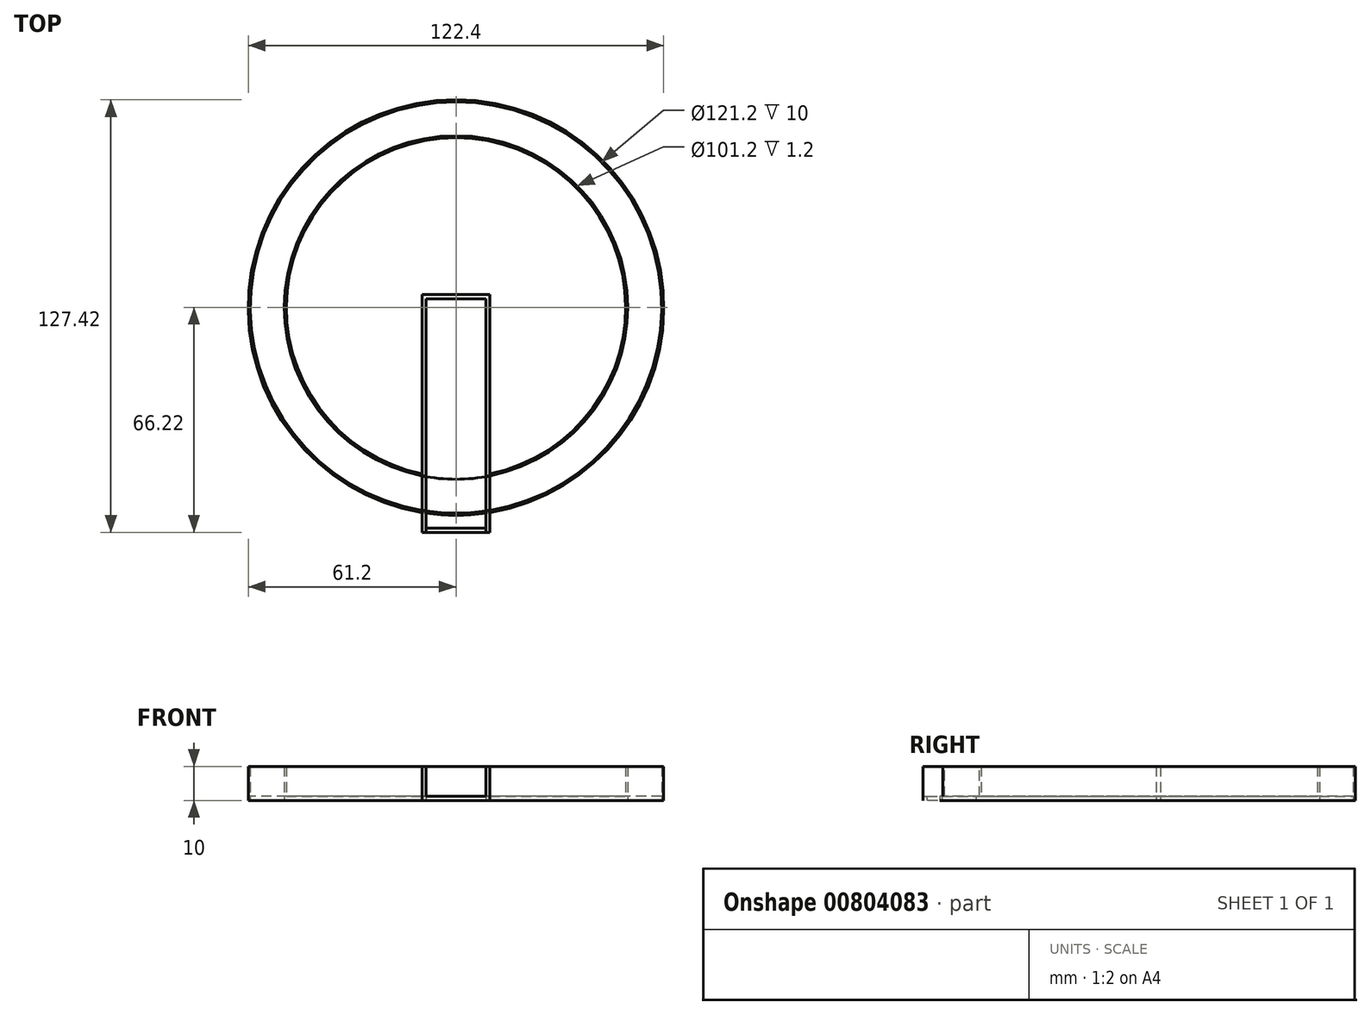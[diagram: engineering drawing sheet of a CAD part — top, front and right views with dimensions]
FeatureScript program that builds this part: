
annotation { "Feature Type Name" : "Feature", "Feature Type Description" : "" }
export const myFeature = defineFeature(function(context is Context, id is Id, definition is map)
    precondition{}
    {
        {
            var Q0;
            Q0=qCreatedBy(makeId("Top.planeOp"),FACE);
            var sketch = newSketch(context, id + "F0", { "sketchPlane" : qUnion([Q0])});
            skCircle(sketch, "E0", {"center": v(0, 0) * mm, "radius": 50 * mm});
            skCircle(sketch, "E1", {"center": v(0, 0) * mm, "radius": 50.6 * mm});
            skSolve(sketch);
        }
        {
            var Q0;
            Q0=qCreatedBy(makeId("Top.planeOp"),FACE);
            var sketch = newSketch(context, id + "F1", { "sketchPlane" : qUnion([Q0])});
            skCircle(sketch, "E2", {"center": v(0, 0) * mm, "radius": 50 * mm});
            skSolve(sketch);
        }
        {
            var Q0;
            Q0=makeQuery(id+"F0.imprint","IMPRINT",FACE,{"disambiguationData":[TD([[makeQuery(id+"F0.imprint","IMPRINT",EDGE,{"derivedFrom":sQuery(id+"F0.wireOp",EDGE,"E0")}),-1.0]])]});
            extrude(context, id + "F2", {"entities" : qUnion([Q0]), "depth" : 10 * mm, "offsetDistance" : 25 * mm});
        }
        {
            var Q0;
            Q0=makeQuery(id+"F1.imprint","IMPRINT",FACE,{"disambiguationData":[TD([[makeQuery(id+"F1.imprint","IMPRINT",EDGE,{"derivedFrom":sQuery(id+"F1.wireOp",EDGE,"E2")}),1.0]])]});
            extrude(context, id + "F3", {"entities" : qUnion([Q0]), "operationType" : NewBodyOperationType.ADD, "depth" : 1.2 * mm, "offsetDistance" : 25 * mm});
        }
        {
            var Q0;
            Q0=qCreatedBy(makeId("Top.planeOp"),FACE);
            var sketch = newSketch(context, id + "F4", { "sketchPlane" : qUnion([Q0])});
            skCircle(sketch, "E3", {"center": v(0, 0) * mm, "radius": 60.6 * mm});
            skCircle(sketch, "E4", {"center": v(0, 0) * mm, "radius": 61.2 * mm});
            skSolve(sketch);
        }
        {
            var Q0;
            Q0=qCreatedBy(makeId("Top.planeOp"),FACE);
            var sketch = newSketch(context, id + "F5", { "sketchPlane" : qUnion([Q0])});
            skCircle(sketch, "E5", {"center": v(0, 0) * mm, "radius": 60.6 * mm});
            skCircle(sketch, "E6", {"center": v(0, 0) * mm, "radius": 50.6 * mm});
            skSolve(sketch);
        }
        {
            var Q0;
            Q0=makeQuery(id+"F4.imprint","IMPRINT",FACE,{"disambiguationData":[TD([[makeQuery(id+"F4.imprint","IMPRINT",EDGE,{"derivedFrom":sQuery(id+"F4.wireOp",EDGE,"E3")}),-1.0]])]});
            extrude(context, id + "F6", {"entities" : qUnion([Q0]), "depth" : 10 * mm, "offsetDistance" : 25 * mm});
        }
        {
            var Q0;
            Q0=makeQuery(id+"F5.imprint","IMPRINT",FACE,{"disambiguationData":[TD([[makeQuery(id+"F5.imprint","IMPRINT",EDGE,{"derivedFrom":sQuery(id+"F5.wireOp",EDGE,"E5")}),1.0]])]});
            extrude(context, id + "F7", {"entities" : qUnion([Q0]), "depth" : 1.2 * mm, "offsetDistance" : 25 * mm});
        }
        {
            var Q0;
            Q0=qCreatedBy(makeId("Front.planeOp"),FACE);
            var sketch = newSketch(context, id + "F8", { "sketchPlane" : qUnion([Q0])});
            skLineSegment(sketch, "E7.bottom", {"start": v(-10, 10) * mm, "end": v(10, 10) * mm});
            skLineSegment(sketch, "E7.top", {"start": v(-10, 1.2) * mm, "end": v(10, 1.2) * mm});
            skLineSegment(sketch, "E7.left", {"start": v(-10, 10) * mm, "end": v(-10, 1.2) * mm});
            skLineSegment(sketch, "E7.right", {"start": v(10, 10) * mm, "end": v(10, 1.2) * mm});
            skPoint(sketch, "E7.middle", {"position": v(0, 5.6) * mm});
            skSolve(sketch);
        }
        {
            var Q0;
            Q0=makeQuery(id+"F8.imprint","IMPRINT",FACE,{"disambiguationData":[TD([[makeQuery(id+"F8.imprint","IMPRINT",EDGE,{"derivedFrom":sQuery(id+"F8.wireOp",EDGE,"E7.bottom")}),-1.0]])]});
            extrude(context, id + "F9", {"entities" : qUnion([Q0]), "operationType" : NewBodyOperationType.REMOVE, "depth" : 80 * mm, "offsetDistance" : 25 * mm});
        }
        {
            var Q0;
            Q0=qCreatedBy(makeId("Top.planeOp"),FACE);
            var sketch = newSketch(context, id + "F10", { "sketchPlane" : qUnion([Q0])});
            skLineSegment(sketch, "E8.bottom", {"start": v(-10, -66.22) * mm, "end": v(10, -66.22) * mm});
            skLineSegment(sketch, "E8.top", {"start": v(-10, 3.78) * mm, "end": v(10, 3.78) * mm});
            skLineSegment(sketch, "E8.left", {"start": v(-10, -66.22) * mm, "end": v(-10, 3.78) * mm});
            skLineSegment(sketch, "E8.right", {"start": v(10, -66.22) * mm, "end": v(10, 3.78) * mm});
            skPoint(sketch, "E8.middle", {"position": v(0, -31.22) * mm});
            skLineSegment(sketch, "E9.bottom", {"start": v(-8.8, 2.58) * mm, "end": v(8.8, 2.58) * mm});
            skLineSegment(sketch, "E9.top", {"start": v(-8.8, -65.02) * mm, "end": v(8.8, -65.02) * mm});
            skLineSegment(sketch, "E9.left", {"start": v(-8.8, 2.58) * mm, "end": v(-8.8, -65.02) * mm});
            skLineSegment(sketch, "E9.right", {"start": v(8.8, 2.58) * mm, "end": v(8.8, -65.02) * mm});
            skSolve(sketch);
        }
        {
            var Q0;
            Q0=makeQuery(id+"F10.imprint","IMPRINT",FACE,{"disambiguationData":[TD([[makeQuery(id+"F10.imprint","IMPRINT",EDGE,{"derivedFrom":sQuery(id+"F10.wireOp",EDGE,"E8.bottom")}),1.0]])]});
            extrude(context, id + "F11", {"entities" : qUnion([Q0]), "depth" : 10 * mm, "offsetDistance" : 25 * mm});
        }
        {
            var Q0;
            Q0=qCreatedBy(makeId("Top.planeOp"),FACE);
            var sketch = newSketch(context, id + "F12", { "sketchPlane" : qUnion([Q0])});
            skLineSegment(sketch, "E10.bottom", {"start": v(-8.8, -65.02) * mm, "end": v(8.8, -65.02) * mm});
            skLineSegment(sketch, "E10.top", {"start": v(-8.8, 2.58) * mm, "end": v(8.8, 2.58) * mm});
            skLineSegment(sketch, "E10.left", {"start": v(-8.8, -65.02) * mm, "end": v(-8.8, 2.58) * mm});
            skLineSegment(sketch, "E10.right", {"start": v(8.8, -65.02) * mm, "end": v(8.8, 2.58) * mm});
            skPoint(sketch, "E10.middle", {"position": v(0, -31.22) * mm});
            skSolve(sketch);
        }
        {
            var Q0;
            Q0=makeQuery(id+"F12.imprint","IMPRINT",FACE,{"disambiguationData":[TD([[makeQuery(id+"F12.imprint","IMPRINT",EDGE,{"derivedFrom":sQuery(id+"F12.wireOp",EDGE,"E10.bottom")}),1.0]])]});
            extrude(context, id + "F13", {"entities" : qUnion([Q0]), "depth" : 1.2 * mm, "offsetDistance" : 25 * mm});
        }
        {
            var Q0;
            Q0=qCreatedBy(makeId("Right.planeOp"),FACE);
            var sketch = newSketch(context, id + "F14", { "sketchPlane" : qUnion([Q0])});
            skLineSegment(sketch, "E11.bottom", {"start": v(-59.77, 10) * mm, "end": v(-49.6, 10) * mm});
            skLineSegment(sketch, "E11.top", {"start": v(-59.77, 1.2) * mm, "end": v(-49.6, 1.2) * mm});
            skLineSegment(sketch, "E11.left", {"start": v(-59.77, 10) * mm, "end": v(-59.77, 1.2) * mm});
            skLineSegment(sketch, "E11.right", {"start": v(-49.6, 10) * mm, "end": v(-49.6, 1.2) * mm});
            skSolve(sketch);
        }
        {
            var Q0;
            Q0=makeQuery(id+"F14.imprint","IMPRINT",FACE,{"disambiguationData":[TD([[makeQuery(id+"F14.imprint","IMPRINT",EDGE,{"derivedFrom":sQuery(id+"F14.wireOp",EDGE,"E11.bottom")}),-1.0]])]});
            extrude(context, id + "F15", {"entities" : qUnion([Q0]), "operationType" : NewBodyOperationType.REMOVE, "depth" : 10 * mm, "offsetDistance" : 25 * mm, "hasSecondDirection" : true, "secondDirectionOppositeDirection" : true, "secondDirectionDepth" : 10 * mm});
        }
        {
            var Q0;
            Q0=qCreatedBy(makeId("Front.planeOp"),FACE);
            var sketch = newSketch(context, id + "F16", { "sketchPlane" : qUnion([Q0])});
            skLineSegment(sketch, "E12.bottom", {"start": v(8.8, 10) * mm, "end": v(-8.8, 10) * mm});
            skLineSegment(sketch, "E12.top", {"start": v(8.8, 1.2) * mm, "end": v(-8.8, 1.2) * mm});
            skLineSegment(sketch, "E12.left", {"start": v(8.8, 10) * mm, "end": v(8.8, 1.2) * mm});
            skLineSegment(sketch, "E12.right", {"start": v(-8.8, 10) * mm, "end": v(-8.8, 1.2) * mm});
            skPoint(sketch, "E12.middle", {"position": v(0, 5.6) * mm});
            skSolve(sketch);
        }
        {
            var Q0;
            Q0=makeQuery(id+"F16.imprint","IMPRINT",FACE,{"disambiguationData":[TD([[makeQuery(id+"F16.imprint","IMPRINT",EDGE,{"derivedFrom":sQuery(id+"F16.wireOp",EDGE,"E12.bottom")}),1.0]])]});
            extrude(context, id + "F17", {"entities" : qUnion([Q0]), "operationType" : NewBodyOperationType.REMOVE, "depth" : 70 * mm, "offsetDistance" : 25 * mm});
        }
    });
